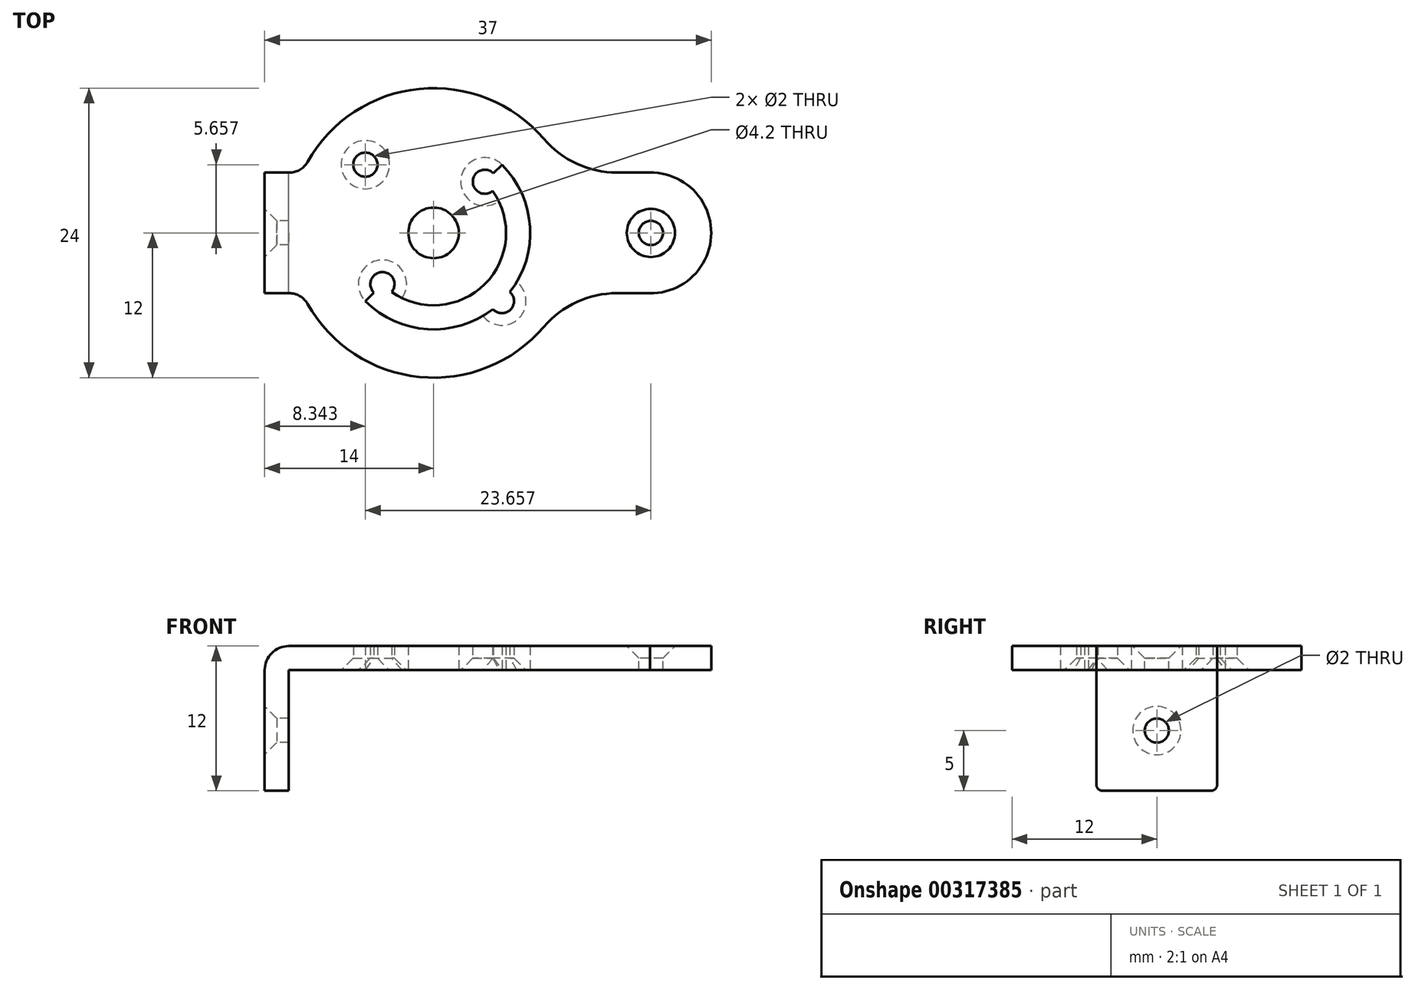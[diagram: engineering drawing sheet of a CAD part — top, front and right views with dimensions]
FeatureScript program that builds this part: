
annotation { "Feature Type Name" : "Feature", "Feature Type Description" : "" }
export const myFeature = defineFeature(function(context is Context, id is Id, definition is map)
    precondition{}
    {
        {
            var Q0;
            Q0=qCreatedBy(makeId("Top.planeOp"),FACE);
            var sketch = newSketch(context, id + "F0", { "sketchPlane" : qUnion([Q0])});
            skCircle(sketch, "E0", {"center": v(0, 0) * mm, "radius": 12 * mm});
            skCircle(sketch, "E1", {"center": v(18, 0) * mm, "radius": 5 * mm});
            skLineSegment(sketch, "E2", {"start": v(17.92, 5) * mm, "end": v(10.9, 5) * mm});
            skLineSegment(sketch, "E3", {"start": v(18.09, -5) * mm, "end": v(10.9, -5) * mm});
            skArc(sketch, "E4", {"start": v(9.12, 7.8) * mm, "mid": v(11.85, 5.73) * mm, "end": v(15.2, 5) * mm});
            skArc(sketch, "E5", {"start": v(15.2, -5) * mm, "mid": v(11.85, -5.73) * mm, "end": v(9.12, -7.8) * mm});
            skCircle(sketch, "E6", {"center": v(0, 0) * mm, "radius": 2.1 * mm});
            skCircle(sketch, "E7", {"center": v(0, 0) * mm, "radius": 6 * mm});
            skCircle(sketch, "E8", {"center": v(0, 0) * mm, "radius": 8 * mm});
            skLineSegment(sketch, "E9", {"start": v(-8.49, 8.49) * mm, "end": v(8.49, -8.49) * mm});
            skLineSegment(sketch, "E10", {"start": v(-8.49, -8.49) * mm, "end": v(8.49, 8.49) * mm});
            skPoint(sketch, "E11", {"position": v(-5.66, 5.66) * mm});
            skPoint(sketch, "E12", {"position": v(5.66, -5.66) * mm});
            skPoint(sketch, "E13", {"position": v(-4.24, -4.24) * mm});
            skPoint(sketch, "E14", {"position": v(4.24, 4.24) * mm});
            skSolve(sketch);
        }
        {
            var Q0;
            Q0 = qSketchRegion(id + "F0", true);
            extrude(context, id + "F1", {"entities" : qUnion([Q0]), "depth" : 2 * mm});
        }
        {
            var Q0;
            Q0=qCreatedBy(makeId("Front.planeOp"),FACE);
            var sketch = newSketch(context, id + "F2", { "sketchPlane" : qUnion([Q0])});
            skLineSegment(sketch, "E15", {"start": v(-12, 0) * mm, "end": v(-12, -10) * mm});
            skLineSegment(sketch, "E16", {"start": v(-12, -10) * mm, "end": v(-14, -10) * mm});
            skLineSegment(sketch, "E17", {"start": v(-14, -10) * mm, "end": v(-14, 0) * mm});
            skArc(sketch, "E18", {"start": v(-14, 0) * mm, "mid": v(-13.41, 1.41) * mm, "end": v(-12, 2) * mm});
            skLineSegment(sketch, "E19", {"start": v(-12, 0) * mm, "end": v(-9, 0) * mm});
            skLineSegment(sketch, "E20", {"start": v(-9, 0) * mm, "end": v(-9, 2) * mm});
            skLineSegment(sketch, "E21", {"start": v(-9, 2) * mm, "end": v(-12, 2) * mm});
            skSolve(sketch);
        }
        {
            var Q0;
            Q0 = qSketchRegion(id + "F2", true);
            extrude(context, id + "F3", {"entities" : qUnion([Q0]), "operationType" : NewBodyOperationType.ADD, "endBound" : BoundingType.SYMMETRIC, "depth" : 10 * mm});
        }
        {
            var Q0;
            Q0=makeQuery(id+"F3.boolean.opBoolean","INTERSECT",EDGE,{"derivedFrom":[makeQuery(id+"F1.opExtrude","SWEPT_FACE",FACE,{"disambiguationData":[OSD([sQuery(id+"F0.wireOp",EDGE,"E0")])]}),makeQuery(id+"F3.opExtrude","CAP_FACE",FACE,{"disambiguationData":[OSD([sQuery(id+"F2.wireOp",EDGE,"E15"),sQuery(id+"F2.wireOp",EDGE,"E16"),sQuery(id+"F2.wireOp",EDGE,"E17"),sQuery(id+"F2.wireOp",EDGE,"E18"),sQuery(id+"F2.wireOp",EDGE,"E19"),sQuery(id+"F2.wireOp",EDGE,"E20"),sQuery(id+"F2.wireOp",EDGE,"E21")])],"isStart":false})]});
            fillet(context, id + "F4", {"entities" : qUnion([Q0]), "radius" : 1.7 * mm, "tangentPropagation" : true, "allowEdgeOverflow" : false});
        }
        {
            var Q0;
            Q0=makeQuery(id+"F3.boolean.opBoolean","INTERSECT",EDGE,{"derivedFrom":[makeQuery(id+"F1.opExtrude","SWEPT_FACE",FACE,{"disambiguationData":[OSD([sQuery(id+"F0.wireOp",EDGE,"E0")])]}),makeQuery(id+"F3.opExtrude","CAP_FACE",FACE,{"disambiguationData":[OSD([sQuery(id+"F2.wireOp",EDGE,"E15"),sQuery(id+"F2.wireOp",EDGE,"E16"),sQuery(id+"F2.wireOp",EDGE,"E17"),sQuery(id+"F2.wireOp",EDGE,"E18"),sQuery(id+"F2.wireOp",EDGE,"E19"),sQuery(id+"F2.wireOp",EDGE,"E20"),sQuery(id+"F2.wireOp",EDGE,"E21")])],"isStart":true})]});
            fillet(context, id + "F5", {"entities" : qUnion([Q0]), "radius" : 1.7 * mm, "tangentPropagation" : true, "allowEdgeOverflow" : false});
        }
        {
            var Q0;
            Q0=makeQuery(id+"F3.boolean.opBoolean","MERGE",FACE,{"derivedFrom":[makeQuery(id+"F1.opExtrude","CAP_FACE",FACE,{"disambiguationData":[OSD([sQuery(id+"F0.wireOp",EDGE,"E0"),sQuery(id+"F0.wireOp",EDGE,"E1"),sQuery(id+"F0.wireOp",EDGE,"E2"),sQuery(id+"F0.wireOp",EDGE,"E3"),sQuery(id+"F0.wireOp",EDGE,"E4"),sQuery(id+"F0.wireOp",EDGE,"E5"),sQuery(id+"F0.wireOp",EDGE,"E6")])],"isStart":false}),makeQuery(id+"F3.opExtrude","SWEPT_FACE",FACE,{"disambiguationData":[OSD([sQuery(id+"F2.wireOp",EDGE,"E21")])]})]});
            var sketch = newSketch(context, id + "F6", { "sketchPlane" : qUnion([Q0])});
            skPoint(sketch, "E22", {"position": v(18, 0) * mm});
            skSolve(sketch);
        }
        {
            var Q0;
            Q0=sQuery(id+"F6.wireOp",VERTEX,"E22");
            var Q1;
            Q1=makeQuery(id+"F1.opExtrude","SWEPT_BODY",BODY,{"disambiguationData":[OSD([sQuery(id+"F0.wireOp",EDGE,"E0"),sQuery(id+"F0.wireOp",EDGE,"E1"),sQuery(id+"F0.wireOp",EDGE,"E2"),sQuery(id+"F0.wireOp",EDGE,"E3"),sQuery(id+"F0.wireOp",EDGE,"E4"),sQuery(id+"F0.wireOp",EDGE,"E5"),sQuery(id+"F0.wireOp",EDGE,"E6")])]});
            hole(context, id + "F7", {"style" : HoleStyle.C_SINK, "endStyle" : HoleEndStyle.THROUGH, "holeDiameter" : 2 * mm, "cSinkDiameter" : 4 * mm, "cSinkAngle" : 90 * degree, "tappedDepth" : 12 * mm, "tapClearance" : 3, "locations" : qUnion([Q0]), "scope" : qUnion([Q1])});
        }
        {
            var Q0;
            {var subQ0=sQuery(id+"F0.wireOp",EDGE,"E9");var subQ1=sQuery(id+"F0.wireOp",EDGE,"E7");var subQ2=makeQuery(id+"F0.imprint","INTERSECT",VERTEX,{"disambiguationData":[OD(0.0)],"derivedFrom":[subQ1,subQ0]});Q0=makeQuery(id+"F0.imprint","IMPRINT",FACE,{"disambiguationData":[TD([[makeQuery(id+"F0.imprint","IMPRINT",EDGE,{"disambiguationData":[TD([[subQ2,-1.0]])],"derivedFrom":subQ1}),-1.0]])]});}
            var Q1;
            {var subQ0=sQuery(id+"F0.wireOp",EDGE,"E9");var subQ1=sQuery(id+"F0.wireOp",EDGE,"E7");var subQ2=makeQuery(id+"F0.imprint","INTERSECT",VERTEX,{"disambiguationData":[OD(0.0)],"derivedFrom":[subQ1,subQ0]});Q1=makeQuery(id+"F0.imprint","IMPRINT",FACE,{"disambiguationData":[TD([[makeQuery(id+"F0.imprint","IMPRINT",EDGE,{"disambiguationData":[TD([[subQ2,1.0]])],"derivedFrom":subQ1}),-1.0]])]});}
            var Q2;
            {var subQ0=sQuery(id+"F0.wireOp",EDGE,"E10");var subQ1=sQuery(id+"F0.wireOp",EDGE,"E7");var subQ2=makeQuery(id+"F0.imprint","INTERSECT",VERTEX,{"disambiguationData":[OD(0.0)],"derivedFrom":[subQ1,subQ0]});Q2=makeQuery(id+"F0.imprint","IMPRINT",FACE,{"disambiguationData":[TD([[makeQuery(id+"F0.imprint","IMPRINT",EDGE,{"disambiguationData":[TD([[subQ2,1.0]])],"derivedFrom":subQ1}),-1.0]])]});}
            var Q3;
            {var subQ0=sQuery(id+"F0.wireOp",EDGE,"E10");var subQ1=sQuery(id+"F0.wireOp",EDGE,"E6");var subQ2=makeQuery(id+"F0.imprint","INTERSECT",VERTEX,{"disambiguationData":[OD(0.0)],"derivedFrom":[subQ1,subQ0]});Q3=makeQuery(id+"F0.imprint","IMPRINT",FACE,{"disambiguationData":[TD([[makeQuery(id+"F0.imprint","IMPRINT",EDGE,{"disambiguationData":[TD([[subQ2,1.0]])],"derivedFrom":subQ1}),-1.0]])]});}
            var Q4;
            {var subQ0=sQuery(id+"F0.wireOp",EDGE,"E10");var subQ1=sQuery(id+"F0.wireOp",EDGE,"E6");var subQ2=makeQuery(id+"F0.imprint","INTERSECT",VERTEX,{"disambiguationData":[OD(1.0)],"derivedFrom":[subQ1,subQ0]});Q4=makeQuery(id+"F0.imprint","IMPRINT",FACE,{"disambiguationData":[TD([[makeQuery(id+"F0.imprint","IMPRINT",EDGE,{"disambiguationData":[TD([[subQ2,-1.0]])],"derivedFrom":subQ1}),-1.0]])]});}
            var Q5;
            {var subQ0=sQuery(id+"F0.wireOp",EDGE,"E9");var subQ1=sQuery(id+"F0.wireOp",EDGE,"E6");var subQ2=makeQuery(id+"F0.imprint","INTERSECT",VERTEX,{"disambiguationData":[OD(0.0)],"derivedFrom":[subQ1,subQ0]});Q5=makeQuery(id+"F0.imprint","IMPRINT",FACE,{"disambiguationData":[TD([[makeQuery(id+"F0.imprint","IMPRINT",EDGE,{"disambiguationData":[TD([[subQ2,-1.0]])],"derivedFrom":subQ1}),-1.0]])]});}
            var Q6;
            {var subQ0=sQuery(id+"F0.wireOp",EDGE,"E9");var subQ1=sQuery(id+"F0.wireOp",EDGE,"E6");var subQ2=makeQuery(id+"F0.imprint","INTERSECT",VERTEX,{"disambiguationData":[OD(0.0)],"derivedFrom":[subQ1,subQ0]});Q6=makeQuery(id+"F0.imprint","IMPRINT",FACE,{"disambiguationData":[TD([[makeQuery(id+"F0.imprint","IMPRINT",EDGE,{"disambiguationData":[TD([[subQ2,1.0]])],"derivedFrom":subQ1}),-1.0]])]});}
            var Q7;
            {var subQ0=sQuery(id+"F0.wireOp",EDGE,"E10");var subQ1=sQuery(id+"F0.wireOp",EDGE,"E7");var subQ2=makeQuery(id+"F0.imprint","INTERSECT",VERTEX,{"disambiguationData":[OD(1.0)],"derivedFrom":[subQ1,subQ0]});Q7=makeQuery(id+"F0.imprint","IMPRINT",FACE,{"disambiguationData":[TD([[makeQuery(id+"F0.imprint","IMPRINT",EDGE,{"disambiguationData":[TD([[subQ2,-1.0]])],"derivedFrom":subQ1}),-1.0]])]});}
            extrude(context, id + "F8", {"entities" : qUnion([Q0, Q1, Q2, Q3, Q4, Q5, Q6, Q7]), "operationType" : NewBodyOperationType.ADD, "depth" : 2 * mm});
        }
        {
            var Q0;
            Q0=sQuery(id+"F0.wireOp",VERTEX,"E13");
            var Q1;
            Q1=sQuery(id+"F0.wireOp",VERTEX,"E12");
            var Q2;
            Q2=sQuery(id+"F0.wireOp",VERTEX,"E14");
            var Q3;
            Q3=sQuery(id+"F0.wireOp",VERTEX,"E11");
            var Q4;
            Q4=makeQuery(id+"F1.opExtrude","SWEPT_BODY",BODY,{"disambiguationData":[OSD([sQuery(id+"F0.wireOp",EDGE,"E0"),sQuery(id+"F0.wireOp",EDGE,"E1"),sQuery(id+"F0.wireOp",EDGE,"E2"),sQuery(id+"F0.wireOp",EDGE,"E3"),sQuery(id+"F0.wireOp",EDGE,"E4"),sQuery(id+"F0.wireOp",EDGE,"E5"),sQuery(id+"F0.wireOp",EDGE,"E8")])]});
            hole(context, id + "F9", {"style" : HoleStyle.C_SINK, "endStyle" : HoleEndStyle.THROUGH, "oppositeDirection" : true, "holeDiameter" : 2 * mm, "cSinkDiameter" : 4 * mm, "cSinkAngle" : 90 * degree, "tappedDepth" : 12 * mm, "tapClearance" : 3, "locations" : qUnion([Q0, Q1, Q2, Q3]), "scope" : qUnion([Q4])});
        }
        {
            var Q0;
            Q0=makeQuery(id+"F3.opExtrude","CAP_EDGE",EDGE,{"disambiguationData":[OSD([sQuery(id+"F2.wireOp",EDGE,"E16")])],"isStart":false});
            var Q1;
            Q1=makeQuery(id+"F3.opExtrude","CAP_EDGE",EDGE,{"disambiguationData":[OSD([sQuery(id+"F2.wireOp",EDGE,"E16")])],"isStart":true});
            fillet(context, id + "F10", {"entities" : qUnion([Q0, Q1]), "radius" : 0.5 * mm, "tangentPropagation" : true, "allowEdgeOverflow" : false});
        }
        {
            var Q0;
            Q0=makeQuery(id+"F3.opExtrude","SWEPT_FACE",FACE,{"disambiguationData":[OSD([sQuery(id+"F2.wireOp",EDGE,"E17")])]});
            var sketch = newSketch(context, id + "F11", { "sketchPlane" : qUnion([Q0])});
            skPoint(sketch, "E23", {"position": v(0, -5) * mm});
            skPoint(sketch, "E23.positionSnap0", {"position": v(0, 0) * mm});
            skSolve(sketch);
        }
        {
            var Q0;
            Q0=sQuery(id+"F11.wireOp",VERTEX,"E23");
            var Q1;
            Q1=makeQuery(id+"F1.opExtrude","SWEPT_BODY",BODY,{"disambiguationData":[OSD([sQuery(id+"F0.wireOp",EDGE,"E0"),sQuery(id+"F0.wireOp",EDGE,"E1"),sQuery(id+"F0.wireOp",EDGE,"E2"),sQuery(id+"F0.wireOp",EDGE,"E3"),sQuery(id+"F0.wireOp",EDGE,"E4"),sQuery(id+"F0.wireOp",EDGE,"E5"),sQuery(id+"F0.wireOp",EDGE,"E8")])]});
            hole(context, id + "F12", {"style" : HoleStyle.C_SINK, "endStyle" : HoleEndStyle.THROUGH, "holeDiameter" : 2 * mm, "cSinkDiameter" : 4 * mm, "cSinkAngle" : 90 * degree, "tappedDepth" : 12 * mm, "tapClearance" : 3, "locations" : qUnion([Q0]), "scope" : qUnion([Q1])});
        }
    });
